# Revit family: Sanitary_Bidets_hansgrohe_62044XXX-EluPura-Q-Wall-hung-Bidet_540_tap-hole_overflow_SmartClean
name_source: partatom
category: Plumbing Fixtures
units: mm (PartAtom-declared; Revit-internal decimal feet)

## family parameters
Cut with Voids When Loaded = No
Host = Face
Maintain Annotation Orientation = No
OmniClass Number = 23.31.23.00
OmniClass Title = Bidets
Part Type = Normal
Room Calculation Point = No
Round Connector Dimension = Use Diameter
Shared = No

## types (1)
- 450 White
    Connector Description = Water Outlet 46 mm
    Default Elevation = 1219 mm
    Description = EluPura Q Wall hung Bidet  540 with tap hole and overflow, HygieneEffect
    Diameter = 46 mm  [stored 0.150919 ft]
    Manufacturer = Hansgrohe
    Material 1 = Hansgrohe - Ceramic - 450 White
    Model = 62044XXX
    Product Page URL = https://www.hansgrohe.com
    Product data url = https://www.bimobject.com
    URL = https://www.hansgrohe.com
    Version = 1

note: [stored X ft] marks values corroborated as IEEE doubles in the binary element streams (Revit-internal decimal feet)

## geometry (parser evidence)
native form markers: Sweep x2
no freeform markers — native parametric forms only
